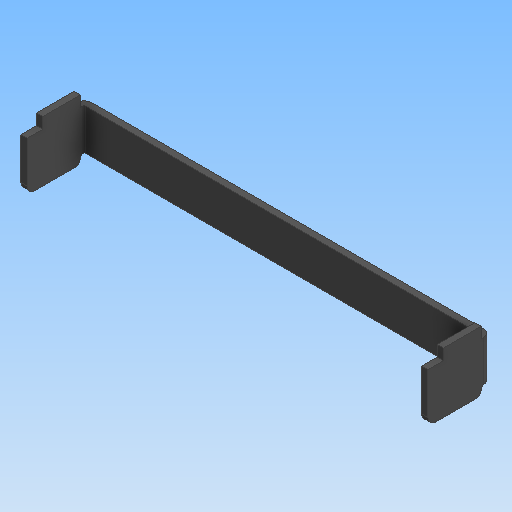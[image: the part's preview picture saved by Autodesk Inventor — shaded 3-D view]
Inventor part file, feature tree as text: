
AUTODESK INVENTOR PART (.ipt)
format: ipt  version: 2020 (Build 240168000, 168)  size: 266,240 bytes
history: native  units: mm
features: other x4, extrude x1
ambient origin geometry x8: Origin, YZ Plane, XZ Plane, XY Plane, X Axis, Y Axis, Z Axis, Center Point
bodies: Body1 (feature_tree)
feature tree (5):
  other  "實體1"
  extrude  "擠出1"  Depth=2.0mm TaperAngle=0.0deg
  other  "折彎零件1"
  other  "折彎零件2"
  other  "定義1"
